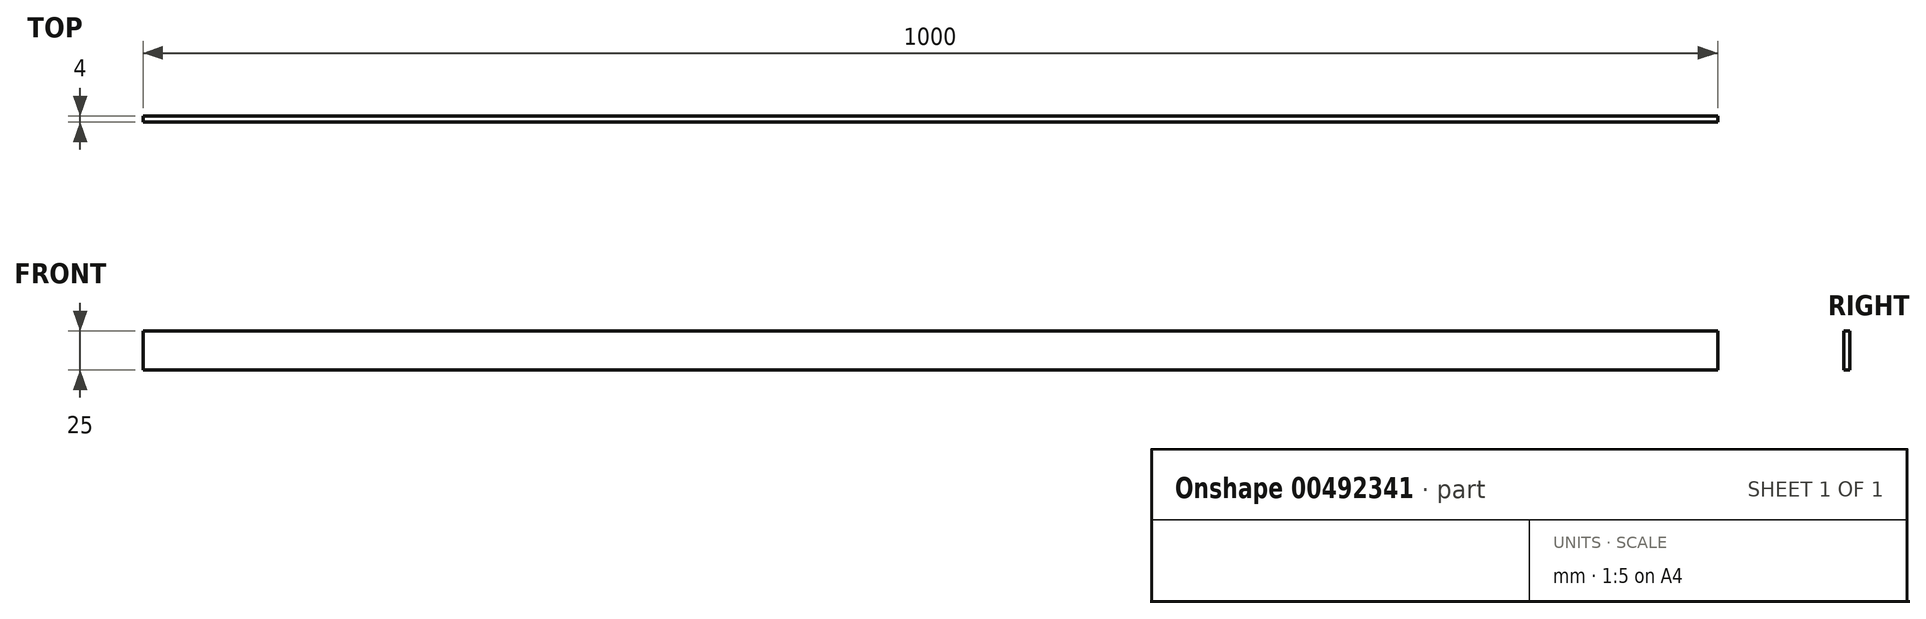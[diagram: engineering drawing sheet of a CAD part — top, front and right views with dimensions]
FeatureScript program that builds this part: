
annotation { "Feature Type Name" : "Feature", "Feature Type Description" : "" }
export const myFeature = defineFeature(function(context is Context, id is Id, definition is map)
    precondition{}
    {
        {
            var Q0;
            Q0=qCreatedBy(makeId("Right.planeOp"),FACE);
            var sketch = newSketch(context, id + "F0", { "sketchPlane" : qUnion([Q0])});
            skLineSegment(sketch, "E0.bottom", {"start": v(0, 13.48) * mm, "end": v(-4, 13.48) * mm});
            skLineSegment(sketch, "E0.top", {"start": v(0, 38.48) * mm, "end": v(-4, 38.48) * mm});
            skLineSegment(sketch, "E0.left", {"start": v(0, 13.48) * mm, "end": v(0, 38.48) * mm});
            skLineSegment(sketch, "E0.right", {"start": v(-4, 13.48) * mm, "end": v(-4, 38.48) * mm});
            skSolve(sketch);
        }
        {
            var Q0;
            Q0=makeQuery(id+"F0.imprint","IMPRINT",FACE,{"disambiguationData":[TD([[makeQuery(id+"F0.imprint","IMPRINT",EDGE,{"derivedFrom":sQuery(id+"F0.wireOp",EDGE,"E0.bottom")}),-1.0]])]});
            extrude(context, id + "F1", {"entities" : qUnion([Q0]), "oppositeDirection" : true, "depth" : 1000 * mm});
        }
    });
